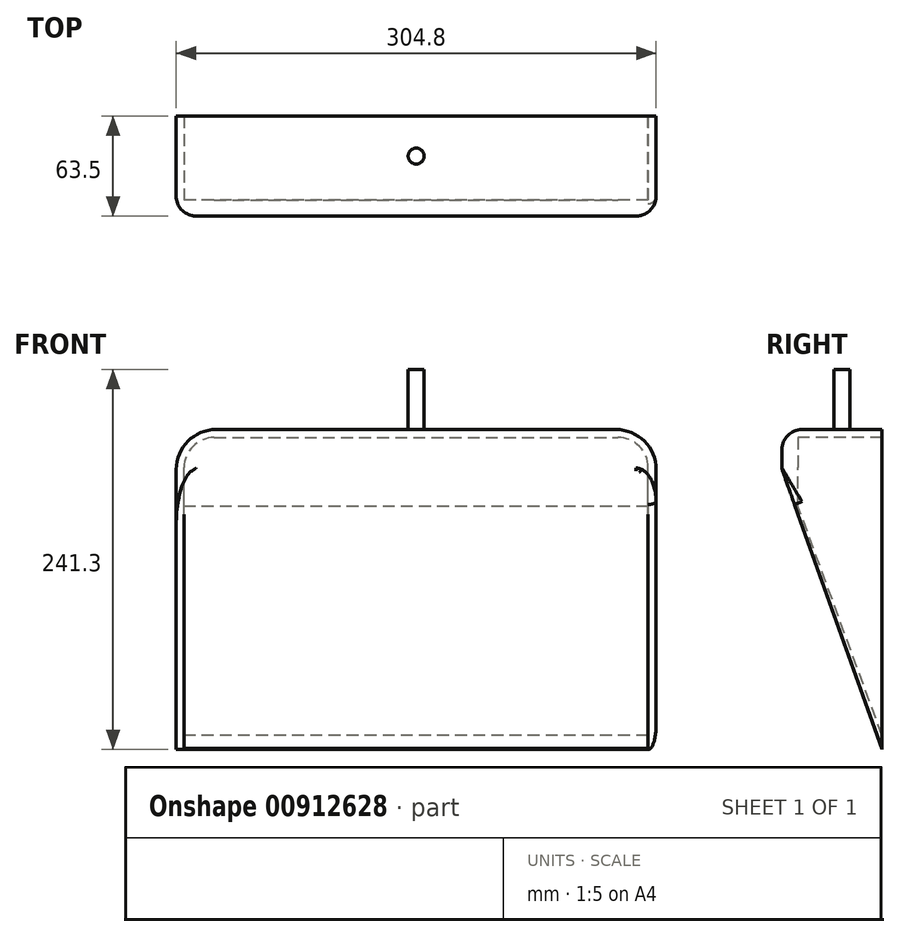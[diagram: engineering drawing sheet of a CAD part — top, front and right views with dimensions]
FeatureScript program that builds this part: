
annotation { "Feature Type Name" : "Feature", "Feature Type Description" : "" }
export const myFeature = defineFeature(function(context is Context, id is Id, definition is map)
    precondition{}
    {
        {
            var Q0;
            Q0=qCreatedBy(makeId("Front.planeOp"),FACE);
            var sketch = newSketch(context, id + "F0", { "sketchPlane" : qUnion([Q0])});
            skLineSegment(sketch, "E0.bottom", {"start": v(-154.42, 149.01) * mm, "end": v(99.58, 149.01) * mm});
            skLineSegment(sketch, "E0.top", {"start": v(-179.82, -54.19) * mm, "end": v(124.98, -54.19) * mm});
            skLineSegment(sketch, "E0.left", {"start": v(-179.82, 123.61) * mm, "end": v(-179.82, -54.19) * mm});
            skLineSegment(sketch, "E0.right", {"start": v(124.98, 123.61) * mm, "end": v(124.98, -54.19) * mm});
            skPoint(sketch, "E1.visualSharp", {"position": v(-179.82, 149.01) * mm});
            skArc(sketch, "E1.filletArc", {"start": v(-154.42, 149.01) * mm, "mid": v(-172.38, 141.57) * mm, "end": v(-179.82, 123.61) * mm});
            skPoint(sketch, "E2.visualSharp", {"position": v(124.98, 149.01) * mm});
            skArc(sketch, "E2.filletArc", {"start": v(124.98, 123.61) * mm, "mid": v(117.54, 141.57) * mm, "end": v(99.58, 149.01) * mm});
            skSolve(sketch);
        }
        {
            var Q0;
            Q0=makeQuery(id+"F0.imprint","IMPRINT",FACE,{"disambiguationData":[TD([[makeQuery(id+"F0.imprint","IMPRINT",EDGE,{"derivedFrom":sQuery(id+"F0.wireOp",EDGE,"E0.bottom")}),-1.0]])]});
            var sketch = newSketch(context, id + "F1", { "sketchPlane" : qUnion([Q0])});
            skLineSegment(sketch, "E3", {"start": v(119.9, -53.94) * mm, "end": v(119.9, 124.8) * mm});
            skLineSegment(sketch, "E4", {"start": v(-155.63, 143.93) * mm, "end": v(100.78, 143.93) * mm});
            skLineSegment(sketch, "E5", {"start": v(-174.76, -53.68) * mm, "end": v(-174.76, 124.8) * mm});
            skPoint(sketch, "E6.visualSharp", {"position": v(-174.76, 143.93) * mm});
            skArc(sketch, "E6.filletArc", {"start": v(-155.63, 143.93) * mm, "mid": v(-169.16, 138.33) * mm, "end": v(-174.76, 124.8) * mm});
            skPoint(sketch, "E7.visualSharp", {"position": v(119.9, 143.93) * mm});
            skArc(sketch, "E7.filletArc", {"start": v(119.9, 124.8) * mm, "mid": v(114.3, 138.33) * mm, "end": v(100.78, 143.93) * mm});
            skLineSegment(sketch, "E8", {"start": v(119.9, -53.94) * mm, "end": v(-174.76, -53.68) * mm});
            skSolve(sketch);
        }
        {
            var Q0;
            Q0=makeQuery(id+"F1.imprint","IMPRINT",FACE,{"disambiguationData":[TD([[makeQuery(id+"F1.imprint","IMPRINT",EDGE,{"derivedFrom":makeQuery(id+"F0.imprint","IMPRINT",EDGE,{"derivedFrom":sQuery(id+"F0.wireOp",EDGE,"E0.bottom")})}),-1.0]])]});
            extrude(context, id + "F2", {"entities" : qUnion([Q0]), "oppositeDirection" : true, "depth" : 63.5 * mm, "offsetDistance" : 25.4 * mm});
        }
        {
            var Q0;
            Q0=makeQuery(id+"F1.imprint","IMPRINT",FACE,{"disambiguationData":[TD([[makeQuery(id+"F1.imprint","IMPRINT",EDGE,{"derivedFrom":sQuery(id+"F1.wireOp",EDGE,"E3")}),1.0]])]});
            extrude(context, id + "F3", {"entities" : qUnion([Q0]), "operationType" : NewBodyOperationType.ADD, "oppositeDirection" : true, "depth" : 10.16 * mm, "offsetDistance" : 25.4 * mm});
        }
        {
            var Q0;
            Q0=makeQuery(id+"F2.opExtrude","SWEPT_FACE",FACE,{"disambiguationData":[OSD([sQuery(id+"F0.wireOp",EDGE,"E0.left")])]});
            var sketch = newSketch(context, id + "F4", { "sketchPlane" : qUnion([Q0])});
            skLineSegment(sketch, "E9", {"start": v(0, 123.61) * mm, "end": v(-63.5, -54.19) * mm});
            skLineSegment(sketch, "E10", {"start": v(-63.5, -54.19) * mm, "end": v(0, -54.19) * mm});
            skLineSegment(sketch, "E11", {"start": v(0, -54.19) * mm, "end": v(0, 123.61) * mm});
            skSolve(sketch);
        }
        {
            var Q0;
            Q0=makeQuery(id+"F4.imprint","IMPRINT",FACE,{"disambiguationData":[TD([[makeQuery(id+"F4.imprint","IMPRINT",EDGE,{"derivedFrom":sQuery(id+"F4.wireOp",EDGE,"E9")}),1.0]])]});
            extrude(context, id + "F5", {"entities" : qUnion([Q0]), "operationType" : NewBodyOperationType.REMOVE, "endBound" : BoundingType.THROUGH_ALL, "oppositeDirection" : true, "depth" : 25.4 * mm, "offsetDistance" : 25.4 * mm});
        }
        {
            var Q0;
            Q0=makeQuery(id+"F2.opExtrude","CAP_EDGE",EDGE,{"disambiguationData":[OSD([sQuery(id+"F0.wireOp",EDGE,"E0.bottom")])],"isStart":true});
            var Q1;
            Q1=makeQuery(id+"F2.opExtrude","CAP_EDGE",EDGE,{"disambiguationData":[OSD([sQuery(id+"F0.wireOp",EDGE,"E1.filletArc")])],"isStart":true});
            var Q2;
            Q2=makeQuery(id+"F2.opExtrude","CAP_EDGE",EDGE,{"disambiguationData":[OSD([sQuery(id+"F0.wireOp",EDGE,"E2.filletArc")])],"isStart":true});
            fillet(context, id + "F6", {"entities" : qUnion([Q0, Q1, Q2]), "radius" : 12.7 * mm, "tangentPropagation" : true, "allowEdgeOverflow" : false});
        }
        {
            var Q0;
            Q0=makeQuery(id+"F2.opExtrude","SWEPT_FACE",FACE,{"disambiguationData":[OSD([sQuery(id+"F0.wireOp",EDGE,"E0.bottom")])]});
            var sketch = newSketch(context, id + "F7", { "sketchPlane" : qUnion([Q0])});
            skCircle(sketch, "E12", {"center": v(-27.42, 38.1) * mm, "radius": 5.08 * mm});
            skSolve(sketch);
        }
        {
            var Q0;
            Q0=makeQuery(id+"F7.imprint","IMPRINT",FACE,{"disambiguationData":[TD([[makeQuery(id+"F7.imprint","IMPRINT",EDGE,{"derivedFrom":sQuery(id+"F7.wireOp",EDGE,"E12")}),1.0]])]});
            extrude(context, id + "F8", {"entities" : qUnion([Q0]), "operationType" : NewBodyOperationType.ADD, "depth" : 38.1 * mm, "offsetDistance" : 25.4 * mm});
        }
        {
            var Q0;
            Q0=makeQuery(id+"F2.opExtrude","SWEPT_FACE",FACE,{"disambiguationData":[OSD([sQuery(id+"F1.wireOp",EDGE,"E5")])]});
            var sketch = newSketch(context, id + "F9", { "sketchPlane" : qUnion([Q0])});
            skLineSegment(sketch, "E13", {"start": v(10.16, 95.16) * mm, "end": v(63.5, -53.68) * mm});
            skLineSegment(sketch, "E14", {"start": v(63.5, -53.68) * mm, "end": v(63.5, -45.35) * mm});
            skLineSegment(sketch, "E15", {"start": v(63.5, -45.35) * mm, "end": v(10.16, 100.19) * mm});
            skLineSegment(sketch, "E16", {"start": v(10.16, 100.19) * mm, "end": v(10.16, 95.16) * mm});
            skSolve(sketch);
        }
        {
            var Q0;
            Q0=makeQuery(id+"F9.imprint","IMPRINT",FACE,{"disambiguationData":[TD([[makeQuery(id+"F9.imprint","IMPRINT",EDGE,{"derivedFrom":sQuery(id+"F9.wireOp",EDGE,"E13")}),1.0]])]});
            extrude(context, id + "F10", {"entities" : qUnion([Q0]), "operationType" : NewBodyOperationType.ADD, "depth" : 297.18 * mm, "offsetDistance" : 25.4 * mm});
        }
        {
            var Q0;
            Q0=makeQuery(id+"F5.boolean.opBoolean","INTERSECT",EDGE,{"derivedFrom":[makeQuery(id+"F2.opExtrude","SWEPT_FACE",FACE,{"disambiguationData":[OSD([sQuery(id+"F0.wireOp",EDGE,"E0.right")])]}),makeQuery(id+"F5.opExtrude","SWEPT_FACE",FACE,{"disambiguationData":[OSD([sQuery(id+"F4.wireOp",EDGE,"E9")])]})]});
            var Q1;
            Q1=makeQuery(id+"F6.opFillet","BLEND_EDGE",EDGE,{"blendedFrom":[makeQuery(id+"F2.opExtrude","CAP_EDGE",EDGE,{"disambiguationData":[OSD([sQuery(id+"F0.wireOp",EDGE,"E2.filletArc")])],"isStart":true}),makeQuery(id+"F5.boolean.opBoolean","COPY",FACE,{"derivedFrom":makeQuery(id+"F5.opExtrude","SWEPT_FACE",FACE,{"disambiguationData":[OSD([sQuery(id+"F4.wireOp",EDGE,"E9")])]})})],"blendedInto":[makeQuery(id+"F5.boolean.opBoolean","COPY",FACE,{"derivedFrom":makeQuery(id+"F5.opExtrude","SWEPT_FACE",FACE,{"disambiguationData":[OSD([sQuery(id+"F4.wireOp",EDGE,"E9")])]})})]});
            fillet(context, id + "F11", {"entities" : qUnion([Q0, Q1]), "radius" : 5.08 * mm, "tangentPropagation" : true, "allowEdgeOverflow" : false});
        }
    });
